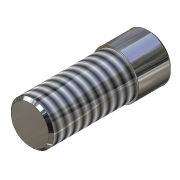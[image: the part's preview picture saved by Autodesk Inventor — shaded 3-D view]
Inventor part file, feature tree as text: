
AUTODESK INVENTOR PART (.ipt)
format: ipt  version: 2016 SP1 (Build 200210100, 210)  size: 123,392 bytes
history: native  units: mm (DEFAULTED — no unit token found)
features: extrude x2, chamfer x2, sketch x2, thread x1, reference x1
ambient origin geometry x8: Origin, YZ Plane, XZ Plane, XY Plane, X Axis, Y Axis, Z Axis, Center Point
bodies: Solid1 (feature_tree)
feature tree (8):
  extrude  "Extrusion1"  Depth=5.08mm TaperAngle=0.0deg
  chamfer  "Chamfer1"  Distance=3.175mm
  extrude  "Extrusion2"  Depth=12.7mm TaperAngle=0.0deg
  chamfer  "Chamfer2"  Distance=3.175mm
  thread  "Thread1"  [1 undecoded]
  sketch  "Sketch1"  dims[d0=6.858mm d1=5.08mm d2=0.0mm d3=0.381mm d4=3.175mm]
  reference  "Reference1"
  sketch  "Sketch2"  dims[d5=6.35mm d6=12.7mm d7=0.0mm d8=0.381mm d9=3.175mm d10=25.4mm d11=0.0mm d12=45.0deg d13=45.0deg]
note: 1 required parameter value undecoded (feature->parameter linkage not recoverable at this tier; creation-order binding heuristic only, values carry confidence <= 0.55)
